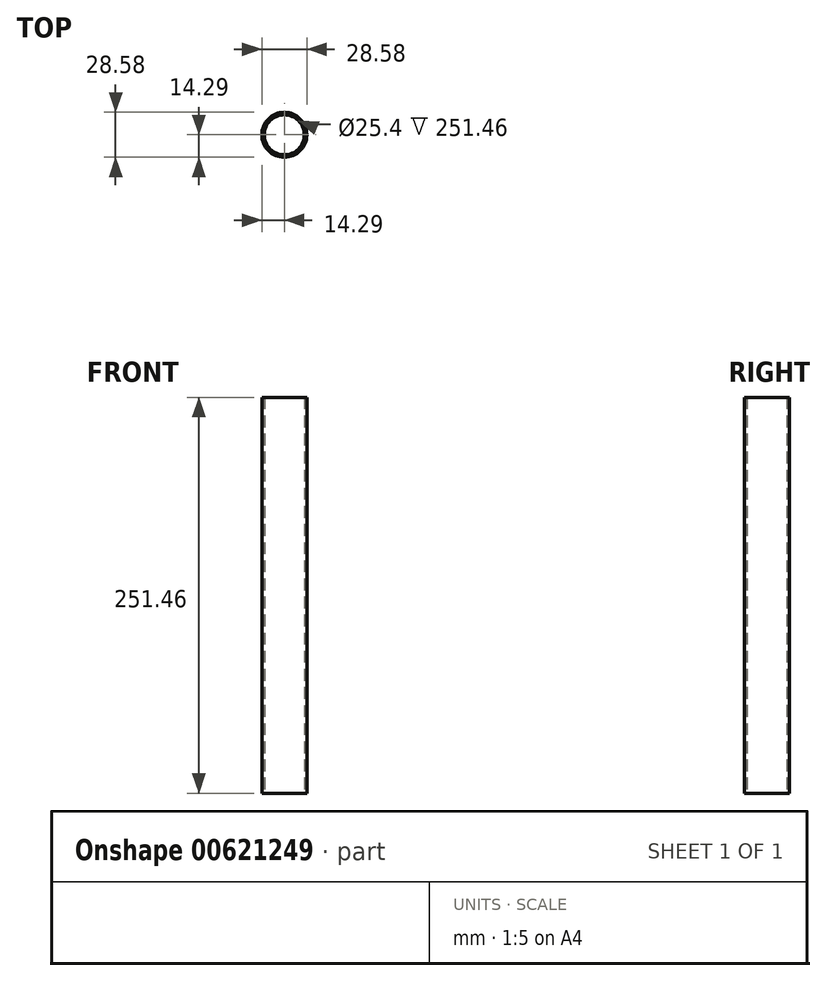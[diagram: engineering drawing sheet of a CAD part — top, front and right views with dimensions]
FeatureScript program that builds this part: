
annotation { "Feature Type Name" : "Feature", "Feature Type Description" : "" }
export const myFeature = defineFeature(function(context is Context, id is Id, definition is map)
    precondition{}
    {
        {
            var Q0;
            Q0=qCreatedBy(makeId("Top.planeOp"),FACE);
            var sketch = newSketch(context, id + "F0", { "sketchPlane" : qUnion([Q0])});
            skLineSegment(sketch, "E0", {"start": v(0, 0) * mm, "end": v(12.7, 0) * mm});
            skCircle(sketch, "E1", {"center": v(0, 0) * mm, "radius": 12.7 * mm});
            skCircle(sketch, "E2.0", {"center": v(0, 0) * mm, "radius": 14.29 * mm});
            skSolve(sketch);
        }
        {
            var Q0;
            Q0=qCreatedBy(makeId("Top.planeOp"),FACE);
            var sketch = newSketch(context, id + "F1", { "sketchPlane" : qUnion([Q0])});
            skSolve(sketch);
        }
        {
            var Q0;
            Q0=qSketchRegion(id+"F1",true);
            var Q1;
            Q1=makeQuery(id+"F0.imprint","IMPRINT",FACE,{"disambiguationData":[TD([[makeQuery(id+"F0.imprint","IMPRINT",EDGE,{"derivedFrom":sQuery(id+"F0.wireOp",EDGE,"E1")}),-1.0]])]});
            extrude(context, id + "F2", {"entities" : qUnion([Q0, Q1]), "depth" : 251.46 * mm, "offsetDistance" : 25.4 * mm});
        }
    });
